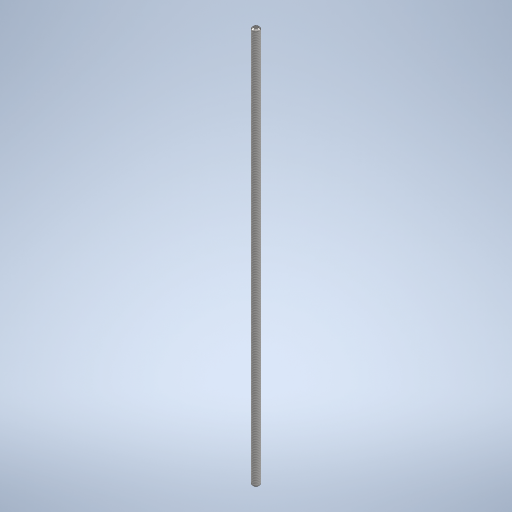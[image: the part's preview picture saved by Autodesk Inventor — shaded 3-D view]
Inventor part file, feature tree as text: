
AUTODESK INVENTOR PART (.ipt)
format: ipt  version: 2024 (Build 280153000, 153)  size: 251,904 bytes
history: native  units: in
note: dims shown in document units (in); Inventor stores cm internally (conversion verified against a paired STEP export)
features: extrude x1, chamfer x1, thread x1, sketch x1
ambient origin geometry x8: Origin, YZ Plane, XZ Plane, XY Plane, X Axis, Y Axis, Z Axis, Center Point
bodies: Solid1 (feature_tree)
feature tree (4):
  extrude  "Extrusion1"  Depth=14.0in TaperAngle=0.0deg
  chamfer  "Chamfer1"  Distance=0.125in Angle=45.0deg
  thread  "Thread1"  [1 undecoded]
  sketch  "Sketch1"  dims[d0=0.25in d1=14.0in d2=0.0in d3=0.05in d4=0.125in d5=45.0deg d6=13.9in d7=0.0in]
note: 1 required parameter value undecoded (feature->parameter linkage not recoverable at this tier; creation-order binding heuristic only, values carry confidence <= 0.55)
